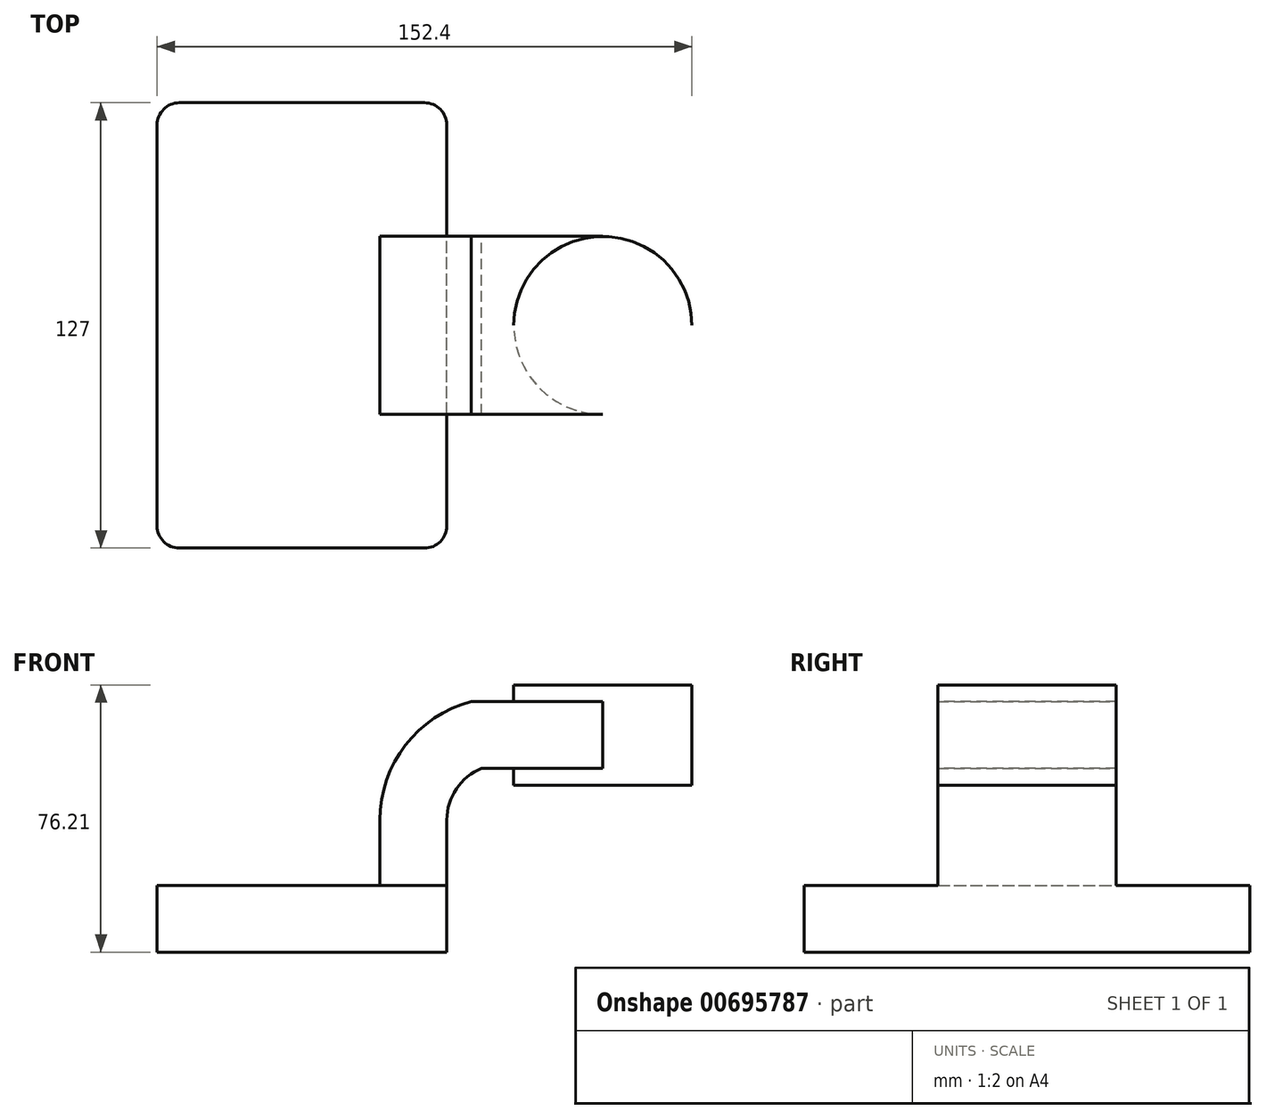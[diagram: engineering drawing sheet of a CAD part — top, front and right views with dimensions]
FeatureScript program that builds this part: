
annotation { "Feature Type Name" : "Feature", "Feature Type Description" : "" }
export const myFeature = defineFeature(function(context is Context, id is Id, definition is map)
    precondition{}
    {
        {
            var Q0;
            Q0=qCreatedBy(makeId("Front.planeOp"),FACE);
            var sketch = newSketch(context, id + "F0", { "sketchPlane" : qUnion([Q0])});
            skLineSegment(sketch, "E0.bottom", {"start": v(-41.28, 9.52) * mm, "end": v(41.27, 9.53) * mm});
            skLineSegment(sketch, "E0.top", {"start": v(-41.28, -9.53) * mm, "end": v(41.28, -9.53) * mm});
            skLineSegment(sketch, "E0.left", {"start": v(-41.28, 9.52) * mm, "end": v(-41.28, -9.53) * mm});
            skLineSegment(sketch, "E0.right", {"start": v(41.27, 9.53) * mm, "end": v(41.28, -9.52) * mm});
            skPoint(sketch, "E0.middle", {"position": v(0, 0) * mm});
            skLineSegment(sketch, "E1.bottom", {"start": v(111.12, 38.1) * mm, "end": v(60.32, 38.1) * mm});
            skLineSegment(sketch, "E1.top", {"start": v(111.12, 66.68) * mm, "end": v(60.32, 66.68) * mm});
            skLineSegment(sketch, "E1.left", {"start": v(111.12, 38.1) * mm, "end": v(111.12, 66.68) * mm});
            skLineSegment(sketch, "E1.right", {"start": v(60.32, 38.1) * mm, "end": v(60.32, 66.68) * mm});
            skPoint(sketch, "E1.middle", {"position": v(85.72, 52.39) * mm});
            skLineSegment(sketch, "E2", {"start": v(41.27, 9.53) * mm, "end": v(41.27, 28.15) * mm});
            skArc(sketch, "E3", {"start": v(41.27, 28.15) * mm, "mid": v(44, 37.03) * mm, "end": v(51.21, 42.88) * mm});
            skLineSegment(sketch, "E4", {"start": v(51.21, 42.88) * mm, "end": v(85.73, 42.88) * mm});
            skLineSegment(sketch, "E5.0", {"start": v(48.25, 61.93) * mm, "end": v(85.73, 61.93) * mm});
            skArc(sketch, "E5.1", {"start": v(22.22, 28.15) * mm, "mid": v(29.49, 49.47) * mm, "end": v(48.25, 61.93) * mm});
            skLineSegment(sketch, "E5.2", {"start": v(22.22, 9.53) * mm, "end": v(22.22, 28.15) * mm});
            skLineSegment(sketch, "E6", {"start": v(85.72, 66.68) * mm, "end": v(85.73, 38.1) * mm});
            skPoint(sketch, "E6.endSnap0", {"position": v(85.72, 38.1) * mm});
            skFitSpline(sketch, "E7", {"points": [v(-41.28, 9.52) * mm, v(48.25, 61.93) * mm], "startDerivative": vector(1.53, 52.04) * mm, "endDerivative": vector(116.8, 3.16) * mm});
            skSolve(sketch);
        }
        {
            var Q0;
            {var subQ1=sQuery(id+"F0.wireOp",EDGE,"E2");Q0=makeQuery(id+"F0.imprint","IMPRINT",FACE,{"disambiguationData":[TD([[makeQuery(id+"F0.imprint","IMPRINT",EDGE,{"derivedFrom":subQ1}),1.0]])]});}
            var Q1;
            {var subQ0=sQuery(id+"F0.wireOp",EDGE,"E4");var subQ1=sQuery(id+"F0.wireOp",EDGE,"E1.right");var subQ2=makeQuery(id+"F0.imprint","INTERSECT",VERTEX,{"derivedFrom":[subQ1,subQ0]});Q1=makeQuery(id+"F0.imprint","IMPRINT",FACE,{"disambiguationData":[TD([[makeQuery(id+"F0.imprint","IMPRINT",EDGE,{"disambiguationData":[TD([[subQ2,-1.0]])],"derivedFrom":subQ1}),-1.0]])]});}
            extrude(context, id + "F1", {"entities" : qUnion([Q0, Q1]), "endBound" : BoundingType.SYMMETRIC, "depth" : 50.8 * mm, "offsetDistance" : 25.4 * mm});
        }
        {
            var Q0;
            Q0=makeQuery(id+"F0.imprint","IMPRINT",FACE,{"disambiguationData":[TD([[makeQuery(id+"F0.imprint","IMPRINT",EDGE,{"derivedFrom":sQuery(id+"F0.wireOp",EDGE,"E0.top")}),1.0]])]});
            extrude(context, id + "F2", {"entities" : qUnion([Q0]), "operationType" : NewBodyOperationType.ADD, "endBound" : BoundingType.SYMMETRIC, "depth" : 127 * mm, "offsetDistance" : 25.4 * mm});
        }
        {
            var Q0;
            Q0=makeQuery(id+"F0.imprint","IMPRINT",FACE,{"disambiguationData":[TD([[makeQuery(id+"F0.imprint","IMPRINT",EDGE,{"derivedFrom":sQuery(id+"F0.wireOp",EDGE,"E5.1")}),1.0]])]});
            extrude(context, id + "F3", {"entities" : qUnion([Q0]), "operationType" : NewBodyOperationType.ADD, "endBound" : BoundingType.SYMMETRIC, "depth" : 15.88 * mm, "offsetDistance" : 25.4 * mm});
        }
        {
            var Q0;
            {var subQ0=sQuery(id+"F0.wireOp",EDGE,"E1.left");Q0=makeQuery(id+"F0.imprint","IMPRINT",FACE,{"disambiguationData":[TD([[makeQuery(id+"F0.imprint","IMPRINT",EDGE,{"derivedFrom":subQ0}),1.0]])]});}
            var Q1;
            Q1=sQuery(id+"F0.wireOp",EDGE,"E6");
            revolve(context, id + "F4", {"operationType" : NewBodyOperationType.ADD, "entities" : qUnion([Q0]), "axis" : qUnion([Q1]), "revolveType" : RevolveType.FULL});
        }
        {
            var Q0;
            Q0=makeQuery(id+"F2.opExtrude","CAP_EDGE",EDGE,{"disambiguationData":[OSD([sQuery(id+"F0.wireOp",EDGE,"E0.left")])],"isStart":false});
            var Q1;
            Q1=makeQuery(id+"F2.opExtrude","CAP_EDGE",EDGE,{"disambiguationData":[OSD([sQuery(id+"F0.wireOp",EDGE,"E0.right")])],"isStart":false});
            var Q2;
            Q2=makeQuery(id+"F2.opExtrude","CAP_EDGE",EDGE,{"disambiguationData":[OSD([sQuery(id+"F0.wireOp",EDGE,"E0.left")])],"isStart":true});
            var Q3;
            Q3=makeQuery(id+"F2.opExtrude","CAP_EDGE",EDGE,{"disambiguationData":[OSD([sQuery(id+"F0.wireOp",EDGE,"E0.right")])],"isStart":true});
            fillet(context, id + "F5", {"entities" : qUnion([Q0, Q1, Q2, Q3]), "radius" : 6.35 * mm, "tangentPropagation" : true, "allowEdgeOverflow" : false});
        }
    });
